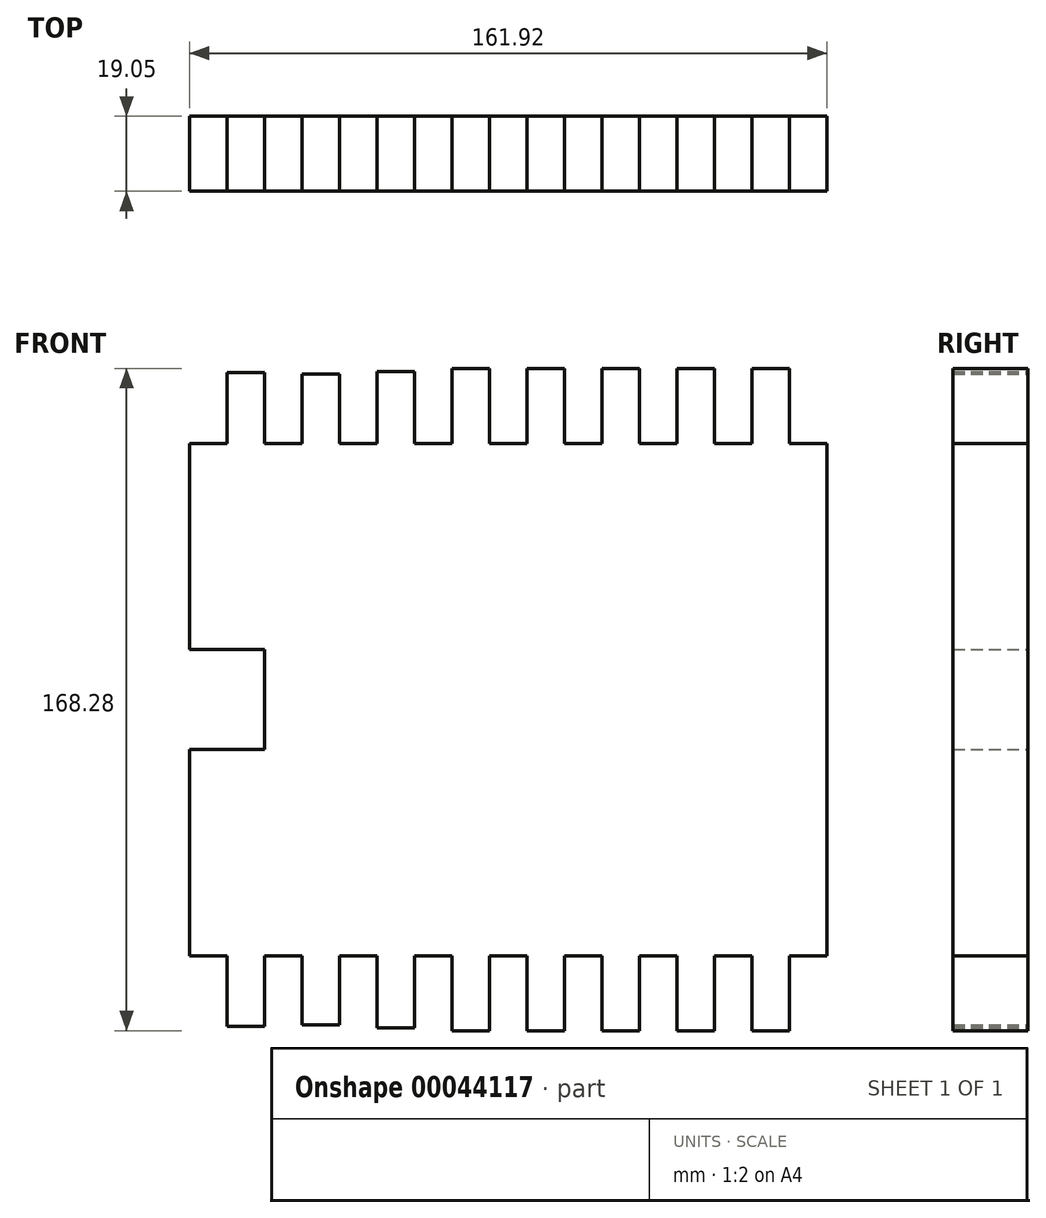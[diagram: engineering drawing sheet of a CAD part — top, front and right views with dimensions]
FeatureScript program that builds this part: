
annotation { "Feature Type Name" : "Feature", "Feature Type Description" : "" }
export const myFeature = defineFeature(function(context is Context, id is Id, definition is map)
    precondition{}
    {
        {
            var Q0;
            Q0=qCreatedBy(makeId("Front.planeOp"),FACE);
            var sketch = newSketch(context, id + "F0", { "sketchPlane" : qUnion([Q0])});
            skLineSegment(sketch, "E0.rect.bottom", {"start": v(80.96, 65.09) * mm, "end": v(71.44, 65.09) * mm});
            skLineSegment(sketch, "E0.rect.left", {"start": v(80.96, 65.09) * mm, "end": v(80.96, -65.09) * mm});
            skLineSegment(sketch, "E0.rect.right", {"start": v(-80.96, 65.09) * mm, "end": v(-80.96, 12.7) * mm});
            skPoint(sketch, "E0.rect.middle", {"position": v(0, 0) * mm});
            skLineSegment(sketch, "E1.rect.bottom", {"start": v(-61.91, 12.7) * mm, "end": v(-80.96, 12.7) * mm});
            skLineSegment(sketch, "E1.rect.top", {"start": v(-61.91, -12.7) * mm, "end": v(-80.96, -12.7) * mm});
            skLineSegment(sketch, "E1.rect.left", {"start": v(-61.91, 12.7) * mm, "end": v(-61.91, -12.7) * mm});
            skLineSegment(sketch, "E2.trimOffspring", {"start": v(-80.96, -12.7) * mm, "end": v(-80.96, -65.09) * mm});
            skLineSegment(sketch, "E3", {"start": v(-14.29, 65.09) * mm, "end": v(-14.29, 84.14) * mm});
            skLineSegment(sketch, "E4", {"start": v(-14.29, 84.14) * mm, "end": v(-4.76, 84.14) * mm});
            skLineSegment(sketch, "E5", {"start": v(-4.76, 84.14) * mm, "end": v(-4.76, 65.09) * mm});
            skLineSegment(sketch, "E6", {"start": v(-4.76, 65.09) * mm, "end": v(4.76, 65.09) * mm});
            skLineSegment(sketch, "E7", {"start": v(4.76, 65.09) * mm, "end": v(4.76, 84.14) * mm});
            skLineSegment(sketch, "E8", {"start": v(4.76, 84.14) * mm, "end": v(14.29, 84.14) * mm});
            skLineSegment(sketch, "E9", {"start": v(14.29, 84.14) * mm, "end": v(14.29, 65.09) * mm});
            skLineSegment(sketch, "E10", {"start": v(33.34, 65.09) * mm, "end": v(42.86, 65.09) * mm});
            skLineSegment(sketch, "E11", {"start": v(42.86, 65.09) * mm, "end": v(42.86, 84.14) * mm});
            skLineSegment(sketch, "E12", {"start": v(42.86, 84.14) * mm, "end": v(52.39, 84.14) * mm});
            skLineSegment(sketch, "E13", {"start": v(52.39, 84.14) * mm, "end": v(52.39, 65.09) * mm});
            skLineSegment(sketch, "E14", {"start": v(52.39, 65.09) * mm, "end": v(61.91, 65.09) * mm});
            skLineSegment(sketch, "E15", {"start": v(61.91, 65.09) * mm, "end": v(61.91, 84.14) * mm});
            skLineSegment(sketch, "E16", {"start": v(61.91, 84.14) * mm, "end": v(71.44, 84.14) * mm});
            skLineSegment(sketch, "E17", {"start": v(71.44, 84.14) * mm, "end": v(71.44, 65.09) * mm});
            skLineSegment(sketch, "E18.trimOffspring", {"start": v(-14.29, 65.09) * mm, "end": v(-23.81, 65.09) * mm});
            skLineSegment(sketch, "E19.trimOffspring", {"start": v(4.76, 65.09) * mm, "end": v(-4.76, 65.09) * mm});
            skLineSegment(sketch, "E20.trimOffspring", {"start": v(42.86, 65.09) * mm, "end": v(33.34, 65.09) * mm});
            skLineSegment(sketch, "E21.trimOffspring", {"start": v(61.91, 65.09) * mm, "end": v(52.39, 65.09) * mm});
            skLineSegment(sketch, "E22", {"start": v(14.29, 65.09) * mm, "end": v(23.81, 65.09) * mm});
            skLineSegment(sketch, "E23", {"start": v(23.81, 65.09) * mm, "end": v(23.81, 84.14) * mm});
            skLineSegment(sketch, "E24", {"start": v(23.81, 84.14) * mm, "end": v(33.34, 84.14) * mm});
            skLineSegment(sketch, "E25", {"start": v(33.34, 84.14) * mm, "end": v(33.34, 65.09) * mm});
            skLineSegment(sketch, "E26", {"start": v(-23.81, 65.09) * mm, "end": v(-23.81, 83.36) * mm});
            skLineSegment(sketch, "E27", {"start": v(-23.81, 83.36) * mm, "end": v(-33.34, 83.36) * mm});
            skLineSegment(sketch, "E28", {"start": v(-33.34, 83.36) * mm, "end": v(-33.34, 65.09) * mm});
            skLineSegment(sketch, "E29", {"start": v(-42.86, 65.09) * mm, "end": v(-42.86, 82.64) * mm});
            skLineSegment(sketch, "E30", {"start": v(-42.86, 82.64) * mm, "end": v(-52.39, 82.64) * mm});
            skLineSegment(sketch, "E31", {"start": v(-52.39, 82.64) * mm, "end": v(-52.39, 65.09) * mm});
            skLineSegment(sketch, "E32", {"start": v(-61.91, 65.09) * mm, "end": v(-61.91, 83.02) * mm});
            skLineSegment(sketch, "E33", {"start": v(-61.91, 83.02) * mm, "end": v(-71.44, 83.02) * mm});
            skLineSegment(sketch, "E34", {"start": v(-71.44, 83.02) * mm, "end": v(-71.44, 65.09) * mm});
            skLineSegment(sketch, "E35.trimOffspring", {"start": v(-71.44, 65.09) * mm, "end": v(-80.96, 65.09) * mm});
            skLineSegment(sketch, "E36.trimOffspring", {"start": v(-52.39, 65.09) * mm, "end": v(-61.91, 65.09) * mm});
            skLineSegment(sketch, "E37.trimOffspring", {"start": v(-33.34, 65.09) * mm, "end": v(-42.86, 65.09) * mm});
            skPoint(sketch, "E38.MirrorCS.start.orphan", {"position": v(80.96, -65.09) * mm});
            skLineSegment(sketch, "E39", {"start": v(-61.91, 0) * mm, "end": v(80.96, 0) * mm, "construction": true});
            skLineSegment(sketch, "E40.MirrorCS", {"start": v(80.96, -65.09) * mm, "end": v(71.44, -65.09) * mm});
            skLineSegment(sketch, "E41.MirrorCS", {"start": v(61.91, -65.09) * mm, "end": v(61.91, -84.14) * mm});
            skLineSegment(sketch, "E42.MirrorCS", {"start": v(61.91, -84.14) * mm, "end": v(71.44, -84.14) * mm});
            skLineSegment(sketch, "E43.MirrorCS", {"start": v(71.44, -84.14) * mm, "end": v(71.44, -65.09) * mm});
            skLineSegment(sketch, "E44.MirrorCS", {"start": v(61.91, -65.09) * mm, "end": v(52.39, -65.09) * mm});
            skLineSegment(sketch, "E45.MirrorCS", {"start": v(42.86, -84.14) * mm, "end": v(52.39, -84.14) * mm});
            skLineSegment(sketch, "E46.MirrorCS", {"start": v(52.39, -84.14) * mm, "end": v(52.39, -65.09) * mm});
            skLineSegment(sketch, "E47.MirrorCS", {"start": v(42.86, -65.09) * mm, "end": v(42.86, -84.14) * mm});
            skLineSegment(sketch, "E48.MirrorCS", {"start": v(33.34, -84.14) * mm, "end": v(33.34, -65.09) * mm});
            skLineSegment(sketch, "E49.MirrorCS", {"start": v(42.86, -65.09) * mm, "end": v(33.34, -65.09) * mm});
            skLineSegment(sketch, "E50.MirrorCS", {"start": v(23.81, -84.14) * mm, "end": v(33.34, -84.14) * mm});
            skLineSegment(sketch, "E51.MirrorCS", {"start": v(23.81, -65.09) * mm, "end": v(23.81, -84.14) * mm});
            skLineSegment(sketch, "E52.MirrorCS", {"start": v(14.29, -65.09) * mm, "end": v(23.81, -65.09) * mm});
            skLineSegment(sketch, "E53.MirrorCS", {"start": v(4.76, -84.14) * mm, "end": v(14.29, -84.14) * mm});
            skLineSegment(sketch, "E54.MirrorCS", {"start": v(4.76, -65.09) * mm, "end": v(4.76, -84.14) * mm});
            skLineSegment(sketch, "E55.MirrorCS", {"start": v(4.76, -65.09) * mm, "end": v(-4.76, -65.09) * mm});
            skLineSegment(sketch, "E56.MirrorCS", {"start": v(14.29, -84.14) * mm, "end": v(14.29, -65.09) * mm});
            skLineSegment(sketch, "E57.MirrorCS", {"start": v(-4.76, -84.14) * mm, "end": v(-4.76, -65.09) * mm});
            skLineSegment(sketch, "E58.MirrorCS", {"start": v(-14.29, -84.14) * mm, "end": v(-4.76, -84.14) * mm});
            skLineSegment(sketch, "E59.MirrorCS", {"start": v(-14.29, -65.09) * mm, "end": v(-23.81, -65.09) * mm});
            skLineSegment(sketch, "E60.MirrorCS", {"start": v(-14.29, -65.09) * mm, "end": v(-14.29, -84.14) * mm});
            skLineSegment(sketch, "E61.MirrorCS", {"start": v(-33.34, -83.36) * mm, "end": v(-33.34, -65.09) * mm});
            skLineSegment(sketch, "E62.MirrorCS", {"start": v(-23.81, -65.09) * mm, "end": v(-23.81, -83.36) * mm});
            skLineSegment(sketch, "E63.MirrorCS", {"start": v(-33.34, -65.09) * mm, "end": v(-42.86, -65.09) * mm});
            skLineSegment(sketch, "E64.MirrorCS", {"start": v(-42.86, -65.09) * mm, "end": v(-42.86, -82.64) * mm});
            skLineSegment(sketch, "E65.MirrorCS", {"start": v(-52.39, -65.09) * mm, "end": v(-61.91, -65.09) * mm});
            skLineSegment(sketch, "E66.MirrorCS", {"start": v(-71.44, -83.02) * mm, "end": v(-71.44, -65.09) * mm});
            skLineSegment(sketch, "E67.MirrorCS", {"start": v(-71.44, -65.09) * mm, "end": v(-80.96, -65.09) * mm});
            skLineSegment(sketch, "E68.MirrorCS", {"start": v(-42.86, -82.64) * mm, "end": v(-52.39, -82.64) * mm});
            skLineSegment(sketch, "E69.MirrorCS", {"start": v(-52.39, -82.64) * mm, "end": v(-52.39, -65.09) * mm});
            skLineSegment(sketch, "E70.MirrorCS", {"start": v(-61.91, -65.09) * mm, "end": v(-61.91, -83.02) * mm});
            skLineSegment(sketch, "E71.MirrorCS", {"start": v(-61.91, -83.02) * mm, "end": v(-71.44, -83.02) * mm});
            skLineSegment(sketch, "E72.MirrorCS", {"start": v(-23.81, -83.36) * mm, "end": v(-33.34, -83.36) * mm});
            skSolve(sketch);
        }
        {
            var Q0;
            {var subQ7=sQuery(id+"F0.wireOp",EDGE,"E0.rect.bottom");Q0=makeQuery(id+"F0.imprint","IMPRINT",FACE,{"disambiguationData":[TD([[makeQuery(id+"F0.imprint","IMPRINT",EDGE,{"derivedFrom":subQ7}),1.0]])]});}
            extrude(context, id + "F1", {"entities" : qUnion([Q0]), "depth" : 19.05 * mm});
        }
    });
